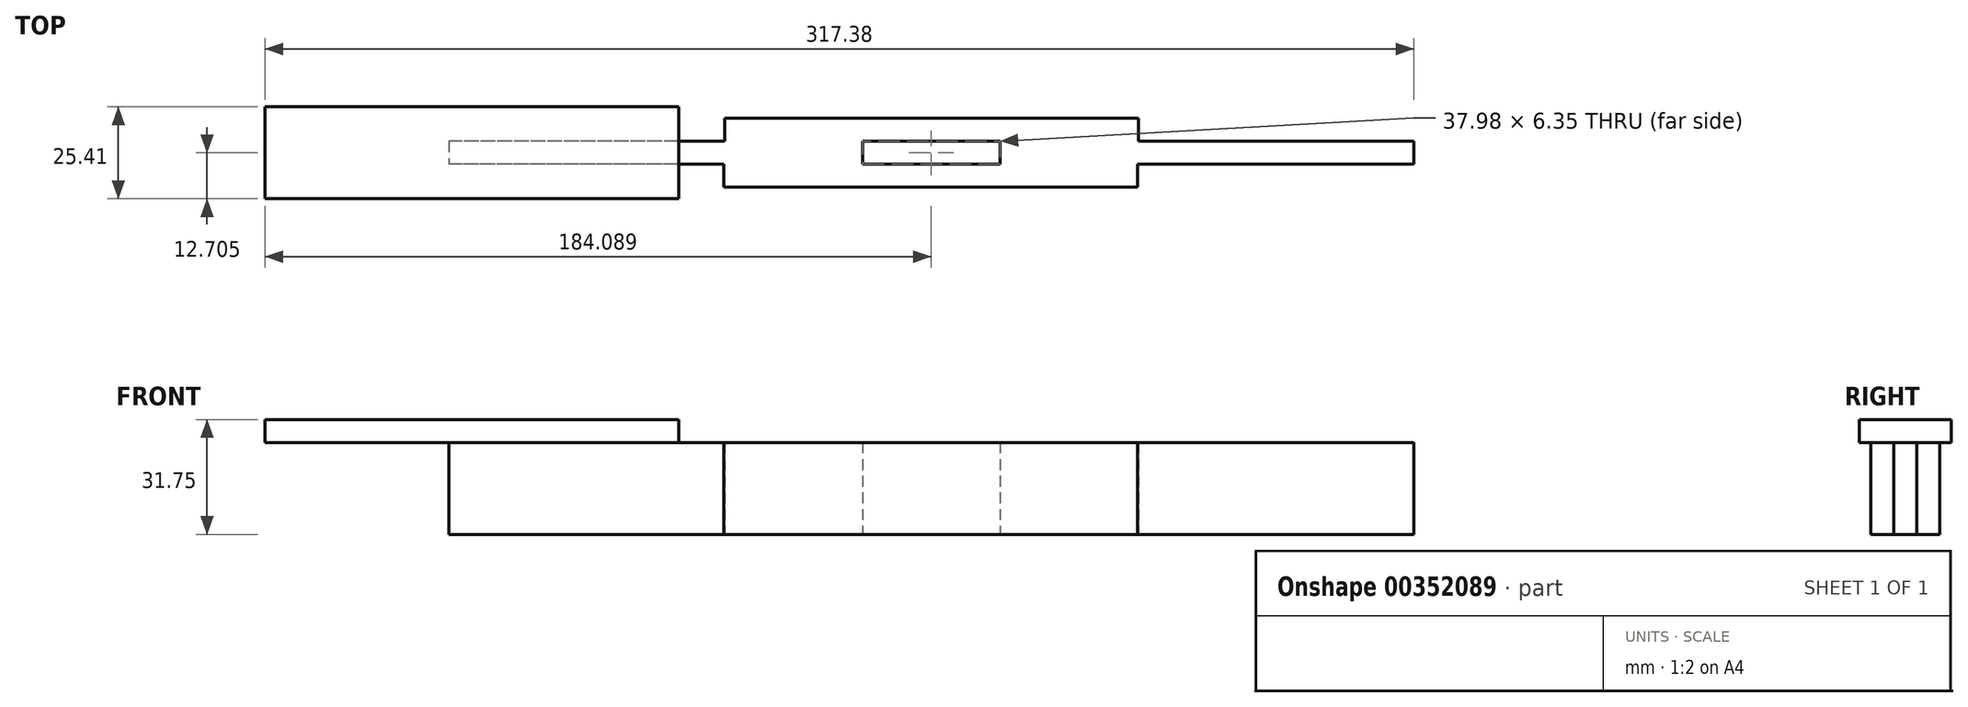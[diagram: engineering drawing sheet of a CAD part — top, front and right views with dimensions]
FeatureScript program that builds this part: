
annotation { "Feature Type Name" : "Feature", "Feature Type Description" : "" }
export const myFeature = defineFeature(function(context is Context, id is Id, definition is map)
    precondition{}
    {
        {
            var Q0;
            Q0=qCreatedBy(makeId("Front.planeOp"),FACE);
            var sketch = newSketch(context, id + "F0", { "sketchPlane" : qUnion([Q0])});
            skLineSegment(sketch, "E0.bottom", {"start": v(0, 0) * mm, "end": v(114.3, 0) * mm});
            skLineSegment(sketch, "E0.top", {"start": v(0, 25.4) * mm, "end": v(114.3, 25.4) * mm});
            skLineSegment(sketch, "E0.left", {"start": v(0, 0) * mm, "end": v(0, 25.4) * mm});
            skLineSegment(sketch, "E0.right", {"start": v(114.3, 0) * mm, "end": v(114.3, 25.4) * mm});
            skSolve(sketch);
        }
        {
            var Q0;
            Q0=qSketchRegion(id+"F0",true);
            extrude(context, id + "F1", {"entities" : qUnion([Q0]), "depth" : 6.35 * mm});
        }
        {
            var Q0;
            Q0=makeQuery(id+"F1.opExtrude","CAP_FACE",FACE,{"disambiguationData":[OSD([sQuery(id+"F0.wireOp",EDGE,"E0.bottom"),sQuery(id+"F0.wireOp",EDGE,"E0.top"),sQuery(id+"F0.wireOp",EDGE,"E0.left"),sQuery(id+"F0.wireOp",EDGE,"E0.right")])],"isStart":true});
            var sketch = newSketch(context, id + "F2", { "sketchPlane" : qUnion([Q0])});
            skLineSegment(sketch, "E1.bottom", {"start": v(-38.34, 25.4) * mm, "end": v(75.96, 25.4) * mm});
            skLineSegment(sketch, "E1.top", {"start": v(-38.34, 0) * mm, "end": v(75.96, 0) * mm});
            skLineSegment(sketch, "E1.left", {"start": v(-38.34, 25.4) * mm, "end": v(-38.34, 0) * mm});
            skLineSegment(sketch, "E1.right", {"start": v(75.96, 25.4) * mm, "end": v(75.96, 0) * mm});
            skSolve(sketch);
        }
        {
            var Q0;
            Q0=qSketchRegion(id+"F2",true);
            extrude(context, id + "F3", {"entities" : qUnion([Q0]), "operationType" : NewBodyOperationType.ADD, "depth" : 6.35 * mm});
        }
        {
            var Q0;
            Q0=makeQuery(id+"F3.opExtrude","CAP_FACE",FACE,{"disambiguationData":[OSD([sQuery(id+"F2.wireOp",EDGE,"E1.bottom"),sQuery(id+"F2.wireOp",EDGE,"E1.top"),sQuery(id+"F2.wireOp",EDGE,"E1.left"),sQuery(id+"F2.wireOp",EDGE,"E1.right")])],"isStart":false});
            var sketch = newSketch(context, id + "F4", { "sketchPlane" : qUnion([Q0])});
            skLineSegment(sketch, "E2.bottom", {"start": v(-0.24, 25.4) * mm, "end": v(-114.54, 25.4) * mm});
            skLineSegment(sketch, "E2.top", {"start": v(-0.24, 0) * mm, "end": v(-114.54, 0) * mm});
            skLineSegment(sketch, "E2.left", {"start": v(-0.24, 25.4) * mm, "end": v(-0.24, 0) * mm});
            skLineSegment(sketch, "E2.right", {"start": v(-114.54, 25.4) * mm, "end": v(-114.54, 0) * mm});
            skSolve(sketch);
        }
        {
            var Q0;
            Q0=qSketchRegion(id+"F4",true);
            extrude(context, id + "F5", {"entities" : qUnion([Q0]), "operationType" : NewBodyOperationType.ADD, "depth" : 6.35 * mm});
        }
        {
            var Q0;
            Q0=makeQuery(id+"F1.opExtrude","CAP_FACE",FACE,{"disambiguationData":[OSD([sQuery(id+"F0.wireOp",EDGE,"E0.bottom"),sQuery(id+"F0.wireOp",EDGE,"E0.top"),sQuery(id+"F0.wireOp",EDGE,"E0.left"),sQuery(id+"F0.wireOp",EDGE,"E0.right")])],"isStart":true});
            var sketch = newSketch(context, id + "F6", { "sketchPlane" : qUnion([Q0])});
            skLineSegment(sketch, "E3.bottom", {"start": v(-76.32, 25.4) * mm, "end": v(-190.62, 25.4) * mm});
            skLineSegment(sketch, "E3.top", {"start": v(-76.32, 0) * mm, "end": v(-190.62, 0) * mm});
            skLineSegment(sketch, "E3.left", {"start": v(-76.32, 25.4) * mm, "end": v(-76.32, 0) * mm});
            skLineSegment(sketch, "E3.right", {"start": v(-190.62, 25.4) * mm, "end": v(-190.62, 0) * mm});
            skSolve(sketch);
        }
        {
            var Q0;
            Q0=qSketchRegion(id+"F6",true);
            extrude(context, id + "F7", {"entities" : qUnion([Q0]), "operationType" : NewBodyOperationType.ADD, "depth" : 6.35 * mm});
        }
        {
            var Q0;
            Q0=makeQuery(id+"F7.boolean.opBoolean","MERGE",FACE,{"derivedFrom":[makeQuery(id+"F5.boolean.opBoolean","MERGE",FACE,{"derivedFrom":[makeQuery(id+"F3.boolean.opBoolean","MERGE",FACE,{"derivedFrom":[makeQuery(id+"F1.opExtrude","SWEPT_FACE",FACE,{"disambiguationData":[OSD([sQuery(id+"F0.wireOp",EDGE,"E0.top")])]}),makeQuery(id+"F3.opExtrude","SWEPT_FACE",FACE,{"disambiguationData":[OSD([sQuery(id+"F2.wireOp",EDGE,"E1.bottom")])]})]}),makeQuery(id+"F5.opExtrude","SWEPT_FACE",FACE,{"disambiguationData":[OSD([sQuery(id+"F4.wireOp",EDGE,"E2.bottom")])]})]}),makeQuery(id+"F7.opExtrude","SWEPT_FACE",FACE,{"disambiguationData":[OSD([sQuery(id+"F6.wireOp",EDGE,"E3.bottom")])]})]});
            var sketch = newSketch(context, id + "F8", { "sketchPlane" : qUnion([Q0])});
            skLineSegment(sketch, "E4", {"start": v(-85.02, 3.18) * mm, "end": v(10.29, 3.18) * mm});
            skLineSegment(sketch, "E5.bottom", {"start": v(-12.46, 3.18) * mm, "end": v(-126.76, 3.18) * mm});
            skLineSegment(sketch, "E5.top", {"start": v(-12.46, 15.88) * mm, "end": v(-126.76, 15.87) * mm});
            skLineSegment(sketch, "E5.left", {"start": v(-12.46, 3.18) * mm, "end": v(-12.46, 15.88) * mm});
            skLineSegment(sketch, "E5.right", {"start": v(-126.76, 3.17) * mm, "end": v(-126.76, 15.87) * mm});
            skLineSegment(sketch, "E6.bottom", {"start": v(-126.76, 3.18) * mm, "end": v(-12.46, 3.18) * mm});
            skLineSegment(sketch, "E6.top", {"start": v(-126.76, -9.52) * mm, "end": v(-12.46, -9.52) * mm});
            skLineSegment(sketch, "E6.left", {"start": v(-126.76, 3.18) * mm, "end": v(-126.76, -9.52) * mm});
            skLineSegment(sketch, "E6.right", {"start": v(-12.46, 3.17) * mm, "end": v(-12.46, -9.52) * mm});
            skSolve(sketch);
        }
        {
            var Q0;
            Q0=qSketchRegion(id+"F8",true);
            extrude(context, id + "F9", {"entities" : qUnion([Q0]), "operationType" : NewBodyOperationType.ADD, "depth" : 6.35 * mm});
        }
    });
